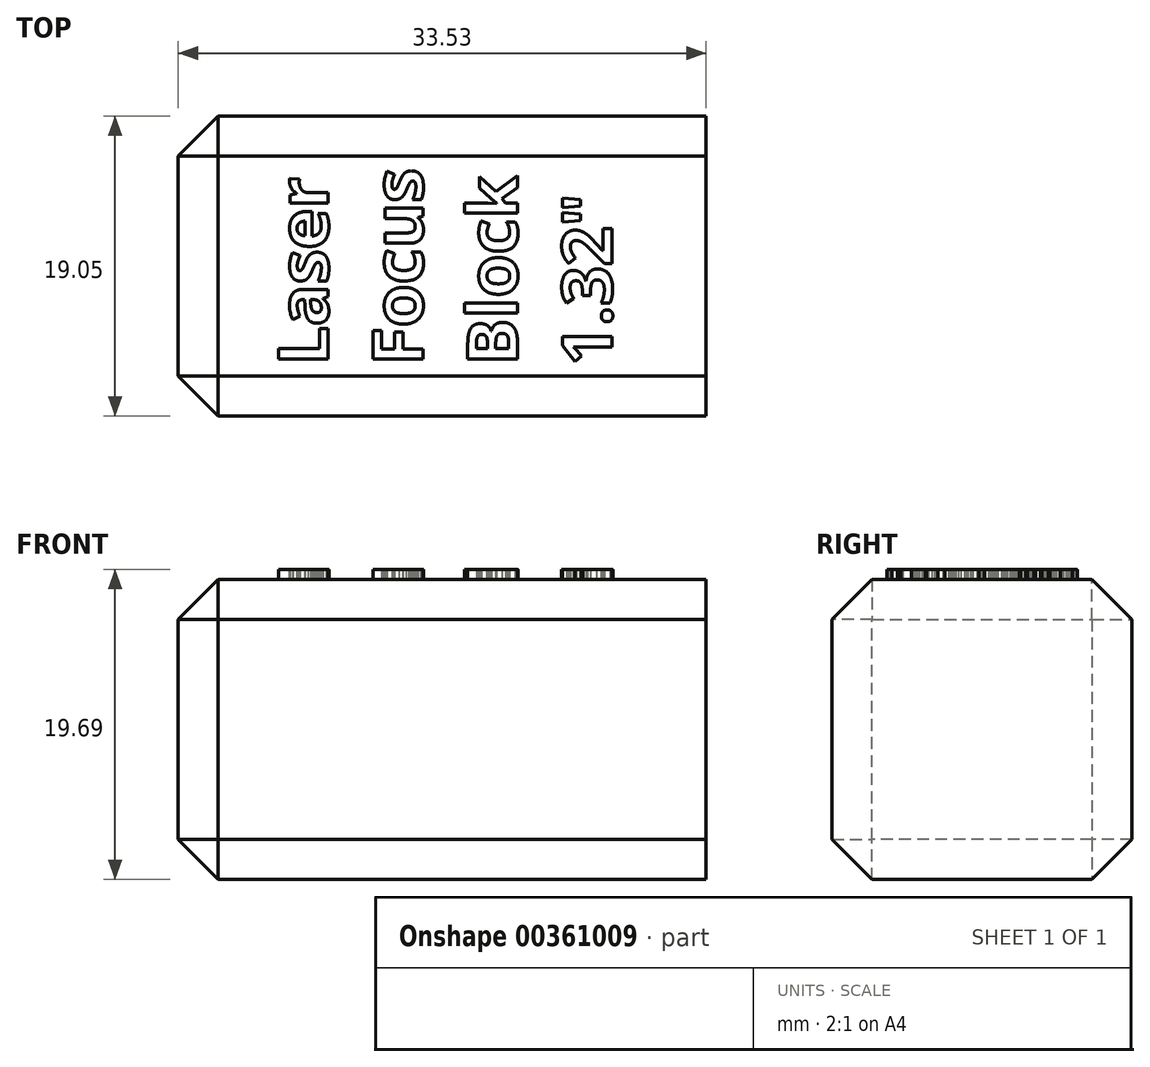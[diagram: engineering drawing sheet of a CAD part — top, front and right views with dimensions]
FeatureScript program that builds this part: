
annotation { "Feature Type Name" : "Feature", "Feature Type Description" : "" }
export const myFeature = defineFeature(function(context is Context, id is Id, definition is map)
    precondition{}
    {
        {
            var Q0;
            Q0=qCreatedBy(makeId("Top.planeOp"),FACE);
            var sketch = newSketch(context, id + "F0", { "sketchPlane" : qUnion([Q0])});
            skLineSegment(sketch, "E0.bottom", {"start": v(0, 0) * mm, "end": v(19.05, 0) * mm});
            skLineSegment(sketch, "E0.top", {"start": v(0, 19.05) * mm, "end": v(19.05, 19.05) * mm});
            skLineSegment(sketch, "E0.left", {"start": v(0, 0) * mm, "end": v(0, 19.05) * mm});
            skLineSegment(sketch, "E0.right", {"start": v(19.05, 0) * mm, "end": v(19.05, 19.05) * mm});
            skSolve(sketch);
        }
        {
            var Q0;
            Q0 = qSketchRegion(id + "F0", true);
            extrude(context, id + "F1", {"entities" : qUnion([Q0]), "depth" : 33.53 * mm});
        }
        {
            var Q0;
            Q0=makeQuery(id+"F1.opExtrude","SWEPT_FACE",FACE,{"disambiguationData":[OSD([sQuery(id+"F0.wireOp",EDGE,"E0.right")])]});
            var sketch = newSketch(context, id + "F2", { "sketchPlane" : qUnion([Q0])});
            skText(sketch, "E1", { "text": "Laser\nFocus\nBlock\n1.32\"", "fontName": "OpenSans-Bold.ttf"});
            skPoint(sketch, "E2", {"position": v(9.52, 33.53) * mm});
            const initialGuessF2  = {"E1": [0.00321, 0.024, 1, 0, 0.00318]};
            skSetInitialGuess(sketch, initialGuessF2);
            skSolve(sketch);
        }
        {
            var Q0;
            Q0 = qSketchRegion(id + "F2", true);
            extrude(context, id + "F3", {"entities" : qUnion([Q0]), "operationType" : NewBodyOperationType.ADD, "depth" : 0.64 * mm});
        }
        {
            var Q0;
            Q0=makeQuery(id+"F1.opExtrude","SWEPT_EDGE",EDGE,{"disambiguationData":[OSD([sQuery(id+"F0.wireOp",EDGE,"E0.bottom"),sQuery(id+"F0.wireOp",EDGE,"E0.right")])]});
            var Q1;
            Q1=makeQuery(id+"F1.opExtrude","SWEPT_EDGE",EDGE,{"disambiguationData":[OSD([sQuery(id+"F0.wireOp",EDGE,"E0.top"),sQuery(id+"F0.wireOp",EDGE,"E0.right")])]});
            var Q2;
            Q2=makeQuery(id+"F1.opExtrude","SWEPT_EDGE",EDGE,{"disambiguationData":[OSD([sQuery(id+"F0.wireOp",EDGE,"E0.bottom"),sQuery(id+"F0.wireOp",EDGE,"E0.left")])]});
            var Q3;
            Q3=makeQuery(id+"F1.opExtrude","SWEPT_EDGE",EDGE,{"disambiguationData":[OSD([sQuery(id+"F0.wireOp",EDGE,"E0.top"),sQuery(id+"F0.wireOp",EDGE,"E0.left")])]});
            var Q4;
            Q4=makeQuery(id+"F1.opExtrude","CAP_EDGE",EDGE,{"disambiguationData":[OSD([sQuery(id+"F0.wireOp",EDGE,"E0.right")])],"isStart":false});
            var Q5;
            Q5=makeQuery(id+"F1.opExtrude","CAP_EDGE",EDGE,{"disambiguationData":[OSD([sQuery(id+"F0.wireOp",EDGE,"E0.left")])],"isStart":false});
            var Q6;
            Q6=makeQuery(id+"F1.opExtrude","CAP_EDGE",EDGE,{"disambiguationData":[OSD([sQuery(id+"F0.wireOp",EDGE,"E0.bottom")])],"isStart":false});
            var Q7;
            Q7=makeQuery(id+"F1.opExtrude","CAP_EDGE",EDGE,{"disambiguationData":[OSD([sQuery(id+"F0.wireOp",EDGE,"E0.top")])],"isStart":false});
            chamfer(context, id + "F4", {"entities" : qUnion([Q0, Q1, Q2, Q3, Q4, Q5, Q6, Q7]), "width" : 2.54 * mm, "tangentPropagation" : true});
        }
        {
            var Q0;
            Q0=makeQuery(id+"F1.opExtrude","SWEPT_BODY",BODY,{"disambiguationData":[OSD([sQuery(id+"F0.wireOp",EDGE,"E0.bottom"),sQuery(id+"F0.wireOp",EDGE,"E0.top"),sQuery(id+"F0.wireOp",EDGE,"E0.left"),sQuery(id+"F0.wireOp",EDGE,"E0.right")])]});
            var Q1;
            Q1=makeQuery(id+"F1.opExtrude","CAP_EDGE",EDGE,{"disambiguationData":[OSD([sQuery(id+"F0.wireOp",EDGE,"E0.right")])],"isStart":true});
            transform(context, id + "F5", {"entities" : qUnion([Q0]), "transformType" : TransformType.ROTATION, "transformAxis" : qUnion([Q1]), "angle" : 270 * degree, "makeCopy" : false});
        }
    });
